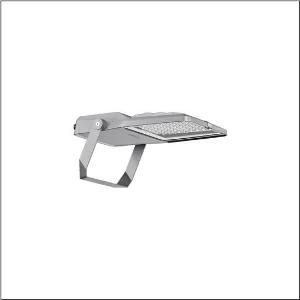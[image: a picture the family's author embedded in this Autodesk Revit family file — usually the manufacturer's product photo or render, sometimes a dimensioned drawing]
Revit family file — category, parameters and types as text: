
# Revit family: floodlight_fl_21_iq_mini___pl33t_5xa7772d1f1a_784a
name_source: partatom
category: Lighting Fixtures
units: mm (PartAtom-declared; Revit-internal decimal feet)

## family parameters
Cut with Voids When Loaded = No
Host = Face
Light Source = No
Part Type = Normal
Room Calculation Point = No
Round Connector Dimension = Use Diameter
Shared = No

## types (1)
- --- (1 x LED, 14590 lm, 143 W, 2200K)
    Apparent Load = 143 VA
    CIE Flux Codes = 26 75 99 100 100
    Color Rendering = 70
    Color Temperature = 2200K
    Default Elevation = 1800 mm
    Description = Floodlight FL 21 iQ mini, floodlight, primary light control with lens, of PMMA, primary optical cover: protective disc, of toughened safety glass, transparent, light distribution: PL33T, light emission: direct distribution, installation type: surface-mounted, LED, High Power LED, rated luminous flux: 14.590lm, luminous efficacy: 102lm/W, light colour: 722, colour temperature: 2200K, control: Street-Remote, Auto-Match, Temp-Guard, Night-Set, Smart-Wire, Desk-Remote (wireless, voltage-free reading and setting of iQ features in the workshop via application-optimized NFC function/RFID function), optimised constant luminous flux control (CLO 2.0), with terminal, 6-pole, mains connection: 220..240V, AC, 50/60Hz, start of lifetime: 143W, end of service life: 152W, reduction: 61W, luminaire housing, of diecast aluminium, powder-coated, Siteco® metallic grey (DB 702S), corrosivity category C5 mid according to DIN EN ISO 12944, sealing non-destructively replaceable, mounting bracket, of steel, galvanised, powder-coated, Siteco® metallic grey (DB 702S), protection rating (complete): IP66, insulation class (complete): insulation class II (safety insulation), certification: CE, ENEC, VDE, protection symbol: D, impact resistance: IK08, permissible operating ambient temperature: -40..+40°C, permissible operating ambient temperature for outdoor applications: -40..+50°C, standard: DIN EN 12944, LABS conformity tested according to VDMA 24364:2018-05, packaging unit: 1 piece

Light Distribution: PL33T
    Height = 70 mm
    Lamp = 1 x LED
    Lamp Light Flux = 14590 lm
    Lamp Power = 143 W
    Lamp count = 1
    Length = 485 mm
    Luminous efficacy = 102 lm/W
    Manufacturer = Siteco
    ModVariant = No
    Model = 5XA7772D1F1A
    Number of Poles = 1
    OnlyDefault = Yes
    Power Factor = 1
    Product Name = Floodlight FL 21 iQ mini | PL33T
    Product group = floodlight | pylon annexe
    ProductGroupID = 6200
    Protection Class = Protection class II
    Protection Degree = IP 66
    RLX_Detail_Level = 1
    RLX_Emergency_Light_Flux = 0 lm
    RLX_Emergency_Type = 0
    RLX_Emergency_Type_DB = No
    RlxData = <blob elided: 96305 chars, md5=c0c7f3c5>
    Socket = socket
    Standby Power = 0 W
    System Light Flux = 14590 lm
    System Power = 143 W
    Type Comments = factory setting: luminous flux: 100 % | dim-lin: 254 | 730 mA
    Type Image = l_1006845.jpg
    URL = http://relux.com
    VarID = @adj_099203
    Voltage = 0 V
    Weight = 0.00 kg
    Width = 337 mm

## geometry (parser evidence)
native form markers: Blend x4, Sweep x13
no freeform markers — native parametric forms only
